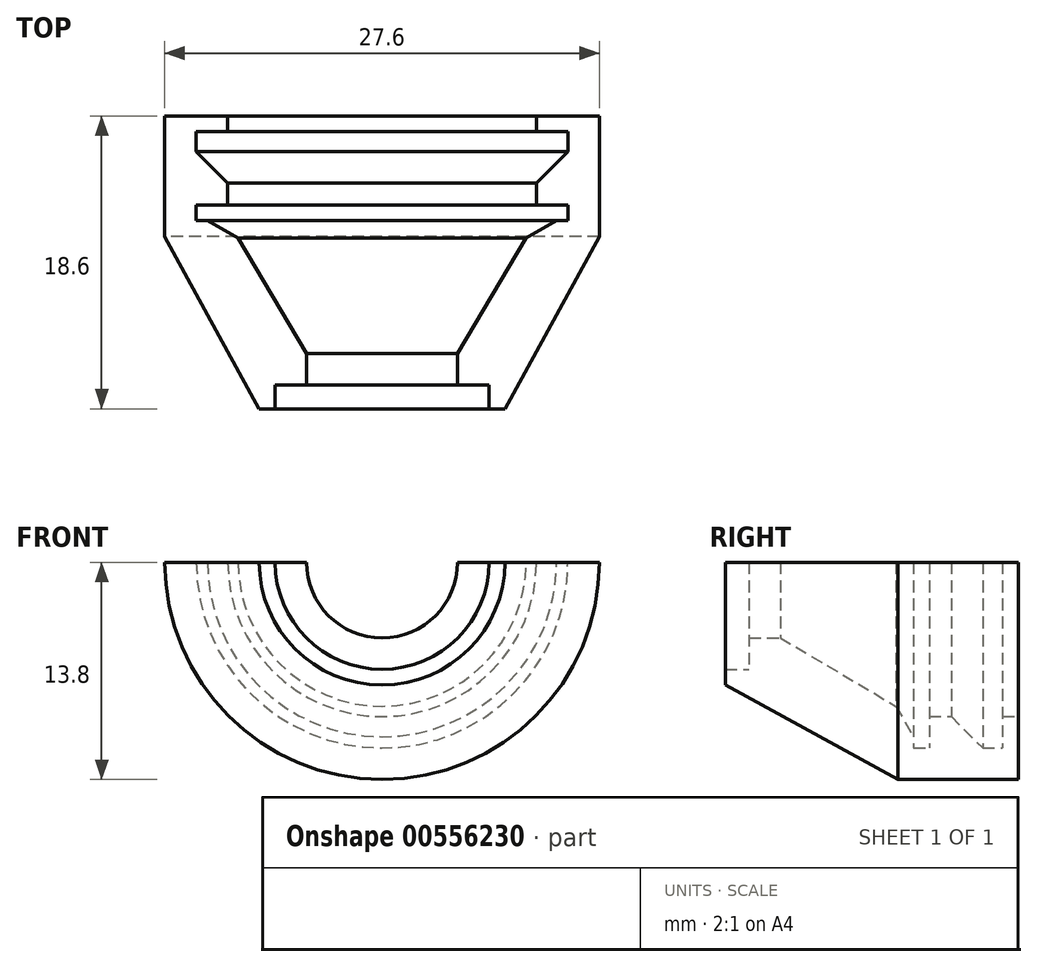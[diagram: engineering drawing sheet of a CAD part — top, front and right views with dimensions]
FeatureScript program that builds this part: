
annotation { "Feature Type Name" : "Feature", "Feature Type Description" : "" }
export const myFeature = defineFeature(function(context is Context, id is Id, definition is map)
    precondition{}
    {
        {
            var Q0;
            Q0=qCreatedBy(makeId("Top.planeOp"),FACE);
            var sketch = newSketch(context, id + "F0", { "sketchPlane" : qUnion([Q0])});
            skLineSegment(sketch, "E0", {"start": v(-11.8, 6.65) * mm, "end": v(-11.8, 5.65) * mm});
            skLineSegment(sketch, "E1", {"start": v(-11.8, 5.65) * mm, "end": v(-9.8, 5.65) * mm});
            skLineSegment(sketch, "E2", {"start": v(-9.8, 2) * mm, "end": v(-11.8, 2) * mm});
            skLineSegment(sketch, "E3", {"start": v(-11.8, 2) * mm, "end": v(-11.8, 1) * mm});
            skLineSegment(sketch, "E4", {"start": v(-11.8, 1) * mm, "end": v(-9.8, 1) * mm});
            skLineSegment(sketch, "E5", {"start": v(-4.8, -9.45) * mm, "end": v(-6.8, -9.45) * mm});
            skLineSegment(sketch, "E6", {"start": v(-6.8, -9.45) * mm, "end": v(-6.8, -10.95) * mm});
            skLineSegment(sketch, "E7", {"start": v(0, 15) * mm, "end": v(0, -15) * mm});
            skLineSegment(sketch, "E8", {"start": v(-9.8, 2) * mm, "end": v(-9.8, 5.65) * mm});
            skLineSegment(sketch, "E9", {"start": v(-13.8, 6.65) * mm, "end": v(-13.8, 0) * mm});
            skLineSegment(sketch, "E10", {"start": v(-13.8, 0) * mm, "end": v(-7.8, -10.95) * mm});
            skLineSegment(sketch, "E11", {"start": v(-4.8, -9.45) * mm, "end": v(-4.8, -7.45) * mm});
            skLineSegment(sketch, "E12", {"start": v(-7.8, -10.95) * mm, "end": v(-6.8, -10.95) * mm});
            skLineSegment(sketch, "E13", {"start": v(-11.8, 6.65) * mm, "end": v(-13.8, 6.65) * mm});
            skLineSegment(sketch, "E14", {"start": v(-9.8, 1) * mm, "end": v(-4.8, -7.45) * mm});
            skLineSegment(sketch, "E15.bottom", {"start": v(-13.8, 6.65) * mm, "end": v(-9.8, 6.65) * mm});
            skLineSegment(sketch, "E15.top", {"start": v(-13.8, 7.65) * mm, "end": v(-9.8, 7.65) * mm});
            skLineSegment(sketch, "E15.left", {"start": v(-13.8, 6.65) * mm, "end": v(-13.8, 7.65) * mm});
            skLineSegment(sketch, "E15.right", {"start": v(-9.8, 6.65) * mm, "end": v(-9.8, 7.65) * mm});
            skSolve(sketch);
        }
        {
            var Q0;
            Q0=makeQuery(id+"F0.imprint","IMPRINT",FACE,{"disambiguationData":[TD([[makeQuery(id+"F0.imprint","IMPRINT",EDGE,{"derivedFrom":sQuery(id+"F0.wireOp",EDGE,"E0")}),-1.0]])]});
            var Q1;
            Q1=makeQuery(id+"F0.imprint","IMPRINT",FACE,{"disambiguationData":[TD([[makeQuery(id+"F0.imprint","IMPRINT",EDGE,{"derivedFrom":sQuery(id+"F0.wireOp",EDGE,"E15.top")}),-1.0]])]});
            var Q2;
            Q2=sQuery(id+"F0.wireOp",EDGE,"E7");
            revolve(context, id + "F1", {"entities" : qUnion([Q0, Q1]), "axis" : qUnion([Q2]), "revolveType" : RevolveType.ONE_DIRECTION, "angle" : 180 * degree});
        }
        {
            var Q0;
            Q0=makeQuery(id+"F1.opRevolve","SWEPT_EDGE",EDGE,{"disambiguationData":[OSD([sQuery(id+"F0.wireOp",EDGE,"E4"),sQuery(id+"F0.wireOp",EDGE,"E14")])]});
            chamfer(context, id + "F2", {"entities" : qUnion([Q0]), "width" : 2.25 * mm, "tangentPropagation" : true});
        }
        {
            var Q0;
            Q0=makeQuery(id+"F1.opRevolve","SWEPT_EDGE",EDGE,{"disambiguationData":[OSD([sQuery(id+"F0.wireOp",EDGE,"E1"),sQuery(id+"F0.wireOp",EDGE,"E8")])]});
            chamfer(context, id + "F3", {"entities" : qUnion([Q0]), "width" : 2.25 * mm, "tangentPropagation" : true});
        }
    });
